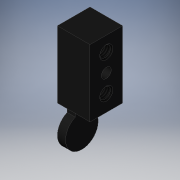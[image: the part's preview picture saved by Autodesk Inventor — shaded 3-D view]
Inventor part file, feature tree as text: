
AUTODESK INVENTOR PART (.ipt)
format: ipt  version: 2019 (Build 230136000, 136)  size: 150,528 bytes
history: native  units: mm
features: other x7, sketch x5, extrude x2, revolve x2, thread x2, hole x1
ambient origin geometry x8: Origin, YZ Plane, XZ Plane, XY Plane, X Axis, Y Axis, Z Axis, Center Point
bodies: Solid1 (feature_tree)
feature tree (19):
  extrude  "Extrusion1"  TaperAngle=360.0deg  [1 undecoded]
  hole  "Hole1"  [1 undecoded]
  revolve  "Revolution1"  [1 undecoded]
  thread  "Thread1"  [1 undecoded]
  revolve  "Revolution2"  [1 undecoded]
  thread  "Thread2"  [1 undecoded]
  extrude  "Extrusion2"  [1 undecoded]
  other  "ANBAU_XY"
  other  "ANBAU_YZ"
  other  "ANBAU_ZX"
  other  "ANBAU_X"
  other  "ANBAU_Y"
  other  "ANBAU_Z"
  other  "ANBAU_Center"
  sketch  "Sketch_11"  dims[d10=9.242mm d11=0.0mm d12=360.0deg]
  sketch  "Sketch2"  dims[d2=3.0mm d3=6.0mm d4=4.0mm d5=2.0mm d6=90.0deg d7=10.0mm d8=0.0mm d9=360.0deg]
  sketch  "Sketch_16"  dims[d13=9.242mm d14=0.0mm d15=2.5mm d16=0.0mm d17=0.0mm]
  sketch  "Sketch_17"
  sketch  "Sketch_1"  dims[d0=10.0mm d1=0.0mm]
note: 7 required parameter values undecoded (feature->parameter linkage not recoverable at this tier; creation-order binding heuristic only, values carry confidence <= 0.55)